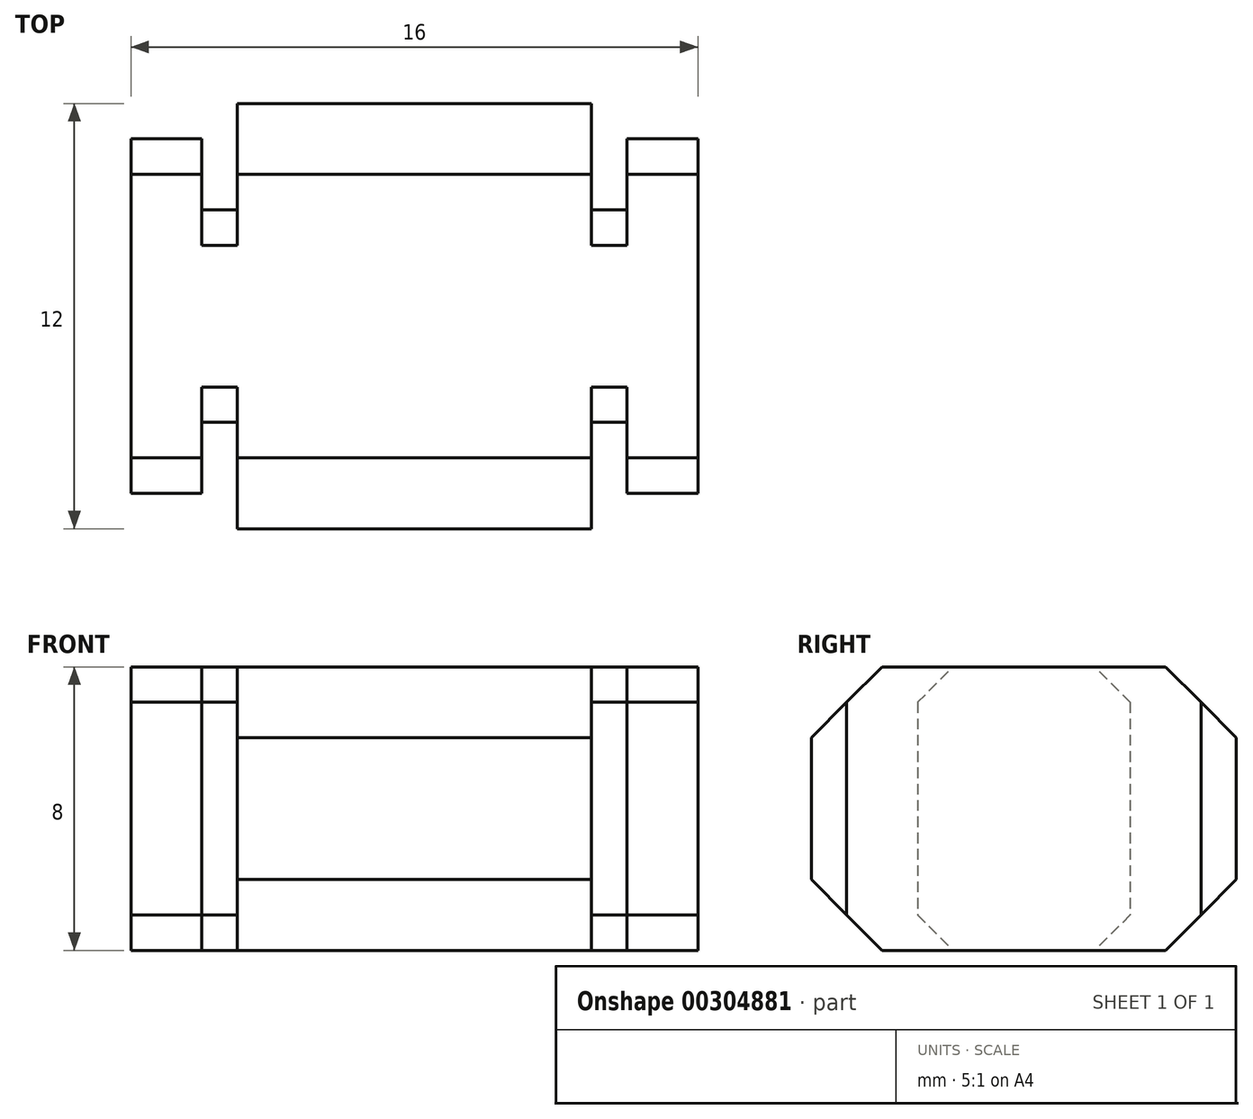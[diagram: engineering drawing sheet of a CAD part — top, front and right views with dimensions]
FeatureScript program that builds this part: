
annotation { "Feature Type Name" : "Feature", "Feature Type Description" : "" }
export const myFeature = defineFeature(function(context is Context, id is Id, definition is map)
    precondition{}
    {
        {
            var Q0;
            Q0=qCreatedBy(makeId("Top.planeOp"),FACE);
            var sketch = newSketch(context, id + "F0", { "sketchPlane" : qUnion([Q0])});
            skLineSegment(sketch, "E0", {"start": v(0, 6) * mm, "end": v(-5, 6) * mm});
            skLineSegment(sketch, "E1", {"start": v(-5, 6) * mm, "end": v(-5, 3) * mm});
            skLineSegment(sketch, "E2", {"start": v(-5, 3) * mm, "end": v(-6, 3) * mm});
            skLineSegment(sketch, "E3", {"start": v(-6, 3) * mm, "end": v(-6, 5) * mm});
            skLineSegment(sketch, "E4", {"start": v(-6, 5) * mm, "end": v(-8, 5) * mm});
            skLineSegment(sketch, "E5", {"start": v(-8, 5) * mm, "end": v(-8, -5) * mm});
            skLineSegment(sketch, "E6", {"start": v(-8, -5) * mm, "end": v(-6, -5) * mm});
            skLineSegment(sketch, "E7", {"start": v(-6, -5) * mm, "end": v(-6, -3) * mm});
            skLineSegment(sketch, "E8", {"start": v(-6, -3) * mm, "end": v(-5, -3) * mm});
            skLineSegment(sketch, "E9", {"start": v(-5, -3) * mm, "end": v(-5, -6) * mm});
            skLineSegment(sketch, "E10", {"start": v(-5, -6) * mm, "end": v(0, -6) * mm});
            skLineSegment(sketch, "E11.MirrorCS", {"start": v(0, 6) * mm, "end": v(5, 6) * mm});
            skLineSegment(sketch, "E12.MirrorCS", {"start": v(5, 6) * mm, "end": v(5, 3) * mm});
            skLineSegment(sketch, "E13.MirrorCS", {"start": v(5, -6) * mm, "end": v(0, -6) * mm});
            skLineSegment(sketch, "E14.MirrorCS", {"start": v(5, 3) * mm, "end": v(6, 3) * mm});
            skLineSegment(sketch, "E15.MirrorCS", {"start": v(6, -5) * mm, "end": v(6, -3) * mm});
            skLineSegment(sketch, "E16.MirrorCS", {"start": v(8, -5) * mm, "end": v(6, -5) * mm});
            skLineSegment(sketch, "E17.MirrorCS", {"start": v(6, 3) * mm, "end": v(6, 5) * mm});
            skLineSegment(sketch, "E18.MirrorCS", {"start": v(6, -3) * mm, "end": v(5, -3) * mm});
            skLineSegment(sketch, "E19.MirrorCS", {"start": v(6, 5) * mm, "end": v(8, 5) * mm});
            skLineSegment(sketch, "E20.MirrorCS", {"start": v(8, 5) * mm, "end": v(8, -5) * mm});
            skLineSegment(sketch, "E21.MirrorCS", {"start": v(5, -3) * mm, "end": v(5, -6) * mm});
            skSolve(sketch);
        }
        {
            var Q0;
            Q0=makeQuery(id+"F0.imprint","IMPRINT",FACE,{"disambiguationData":[TD([[makeQuery(id+"F0.imprint","IMPRINT",EDGE,{"derivedFrom":sQuery(id+"F0.wireOp",EDGE,"E0")}),1.0]])]});
            extrude(context, id + "F1", {"entities" : qUnion([Q0]), "depth" : 8 * mm});
        }
        {
            var Q0;
            Q0=makeQuery(id+"F1.opExtrude","CAP_EDGE",EDGE,{"disambiguationData":[OSD([sQuery(id+"F0.wireOp",EDGE,"E6")])],"isStart":true});
            var Q1;
            Q1=makeQuery(id+"F1.opExtrude","CAP_EDGE",EDGE,{"disambiguationData":[OSD([sQuery(id+"F0.wireOp",EDGE,"E4")])],"isStart":true});
            var Q2;
            Q2=makeQuery(id+"F1.opExtrude","CAP_EDGE",EDGE,{"disambiguationData":[OSD([sQuery(id+"F0.wireOp",EDGE,"E16.MirrorCS")])],"isStart":true});
            var Q3;
            Q3=makeQuery(id+"F1.opExtrude","CAP_EDGE",EDGE,{"disambiguationData":[OSD([sQuery(id+"F0.wireOp",EDGE,"E19.MirrorCS")])],"isStart":true});
            var Q4;
            Q4=makeQuery(id+"F1.opExtrude","CAP_EDGE",EDGE,{"disambiguationData":[OSD([sQuery(id+"F0.wireOp",EDGE,"E6")])],"isStart":false});
            var Q5;
            Q5=makeQuery(id+"F1.opExtrude","CAP_EDGE",EDGE,{"disambiguationData":[OSD([sQuery(id+"F0.wireOp",EDGE,"E4")])],"isStart":false});
            var Q6;
            Q6=makeQuery(id+"F1.opExtrude","CAP_EDGE",EDGE,{"disambiguationData":[OSD([sQuery(id+"F0.wireOp",EDGE,"E16.MirrorCS")])],"isStart":false});
            var Q7;
            Q7=makeQuery(id+"F1.opExtrude","CAP_EDGE",EDGE,{"disambiguationData":[OSD([sQuery(id+"F0.wireOp",EDGE,"E19.MirrorCS")])],"isStart":false});
            var Q8;
            Q8=makeQuery(id+"F1.opExtrude","CAP_EDGE",EDGE,{"disambiguationData":[OSD([sQuery(id+"F0.wireOp",EDGE,"E18.MirrorCS")])],"isStart":false});
            var Q9;
            Q9=makeQuery(id+"F1.opExtrude","CAP_EDGE",EDGE,{"disambiguationData":[OSD([sQuery(id+"F0.wireOp",EDGE,"E14.MirrorCS")])],"isStart":false});
            var Q10;
            Q10=makeQuery(id+"F1.opExtrude","CAP_EDGE",EDGE,{"disambiguationData":[OSD([sQuery(id+"F0.wireOp",EDGE,"E8")])],"isStart":false});
            var Q11;
            Q11=makeQuery(id+"F1.opExtrude","CAP_EDGE",EDGE,{"disambiguationData":[OSD([sQuery(id+"F0.wireOp",EDGE,"E2")])],"isStart":false});
            var Q12;
            Q12=makeQuery(id+"F1.opExtrude","CAP_EDGE",EDGE,{"disambiguationData":[OSD([sQuery(id+"F0.wireOp",EDGE,"E8")])],"isStart":true});
            var Q13;
            Q13=makeQuery(id+"F1.opExtrude","CAP_EDGE",EDGE,{"disambiguationData":[OSD([sQuery(id+"F0.wireOp",EDGE,"E2")])],"isStart":true});
            var Q14;
            Q14=makeQuery(id+"F1.opExtrude","CAP_EDGE",EDGE,{"disambiguationData":[OSD([sQuery(id+"F0.wireOp",EDGE,"E14.MirrorCS")])],"isStart":true});
            var Q15;
            Q15=makeQuery(id+"F1.opExtrude","CAP_EDGE",EDGE,{"disambiguationData":[OSD([sQuery(id+"F0.wireOp",EDGE,"E18.MirrorCS")])],"isStart":true});
            chamfer(context, id + "F2", {"entities" : qUnion([Q0, Q1, Q2, Q3, Q4, Q5, Q6, Q7, Q8, Q9, Q10, Q11, Q12, Q13, Q14, Q15]), "width" : 1 * mm, "tangentPropagation" : true});
        }
        {
            var Q0;
            Q0=makeQuery(id+"F1.opExtrude","CAP_EDGE",EDGE,{"disambiguationData":[OSD([sQuery(id+"F0.wireOp",EDGE,"E10"),sQuery(id+"F0.wireOp",EDGE,"E13.MirrorCS")])],"isStart":false});
            var Q1;
            Q1=makeQuery(id+"F1.opExtrude","CAP_EDGE",EDGE,{"disambiguationData":[OSD([sQuery(id+"F0.wireOp",EDGE,"E10"),sQuery(id+"F0.wireOp",EDGE,"E13.MirrorCS")])],"isStart":true});
            var Q2;
            Q2=makeQuery(id+"F1.opExtrude","CAP_EDGE",EDGE,{"disambiguationData":[OSD([sQuery(id+"F0.wireOp",EDGE,"E0"),sQuery(id+"F0.wireOp",EDGE,"E11.MirrorCS")])],"isStart":false});
            var Q3;
            Q3=makeQuery(id+"F1.opExtrude","CAP_EDGE",EDGE,{"disambiguationData":[OSD([sQuery(id+"F0.wireOp",EDGE,"E0"),sQuery(id+"F0.wireOp",EDGE,"E11.MirrorCS")])],"isStart":true});
            chamfer(context, id + "F3", {"entities" : qUnion([Q0, Q1, Q2, Q3]), "width" : 2 * mm, "tangentPropagation" : true});
        }
    });
